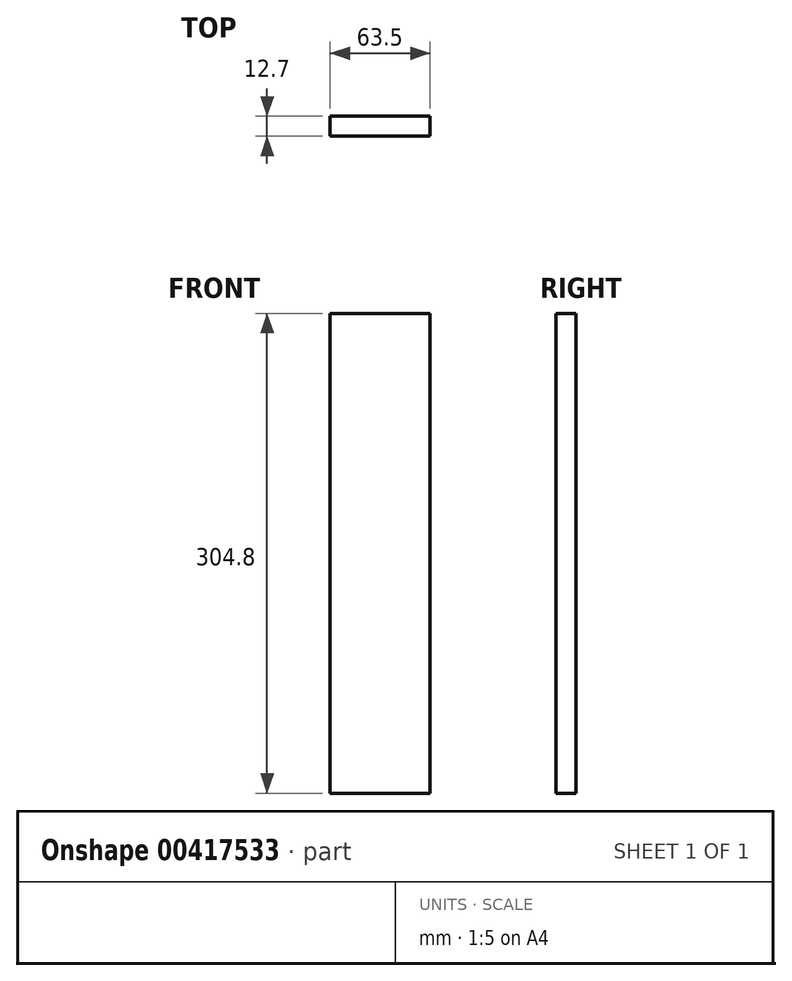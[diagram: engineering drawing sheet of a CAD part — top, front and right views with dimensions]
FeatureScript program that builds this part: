
annotation { "Feature Type Name" : "Feature", "Feature Type Description" : "" }
export const myFeature = defineFeature(function(context is Context, id is Id, definition is map)
    precondition{}
    {
        {
            var Q0;
            Q0=qCreatedBy(makeId("Front.planeOp"),FACE);
            var sketch = newSketch(context, id + "F0", { "sketchPlane" : qUnion([Q0])});
            skLineSegment(sketch, "E0.bottom", {"start": v(-31.75, 152.4) * mm, "end": v(31.75, 152.4) * mm});
            skLineSegment(sketch, "E0.top", {"start": v(-31.75, -152.4) * mm, "end": v(31.75, -152.4) * mm});
            skLineSegment(sketch, "E0.left", {"start": v(-31.75, 152.4) * mm, "end": v(-31.75, -152.4) * mm});
            skLineSegment(sketch, "E0.right", {"start": v(31.75, 152.4) * mm, "end": v(31.75, -152.4) * mm});
            skPoint(sketch, "E0.middle", {"position": v(0, 0) * mm});
            skSolve(sketch);
        }
        {
            var Q0;
            Q0=qSketchRegion(id+"F0",true);
            extrude(context, id + "F1", {"entities" : qUnion([Q0]), "depth" : 12.7 * mm});
        }
    });
